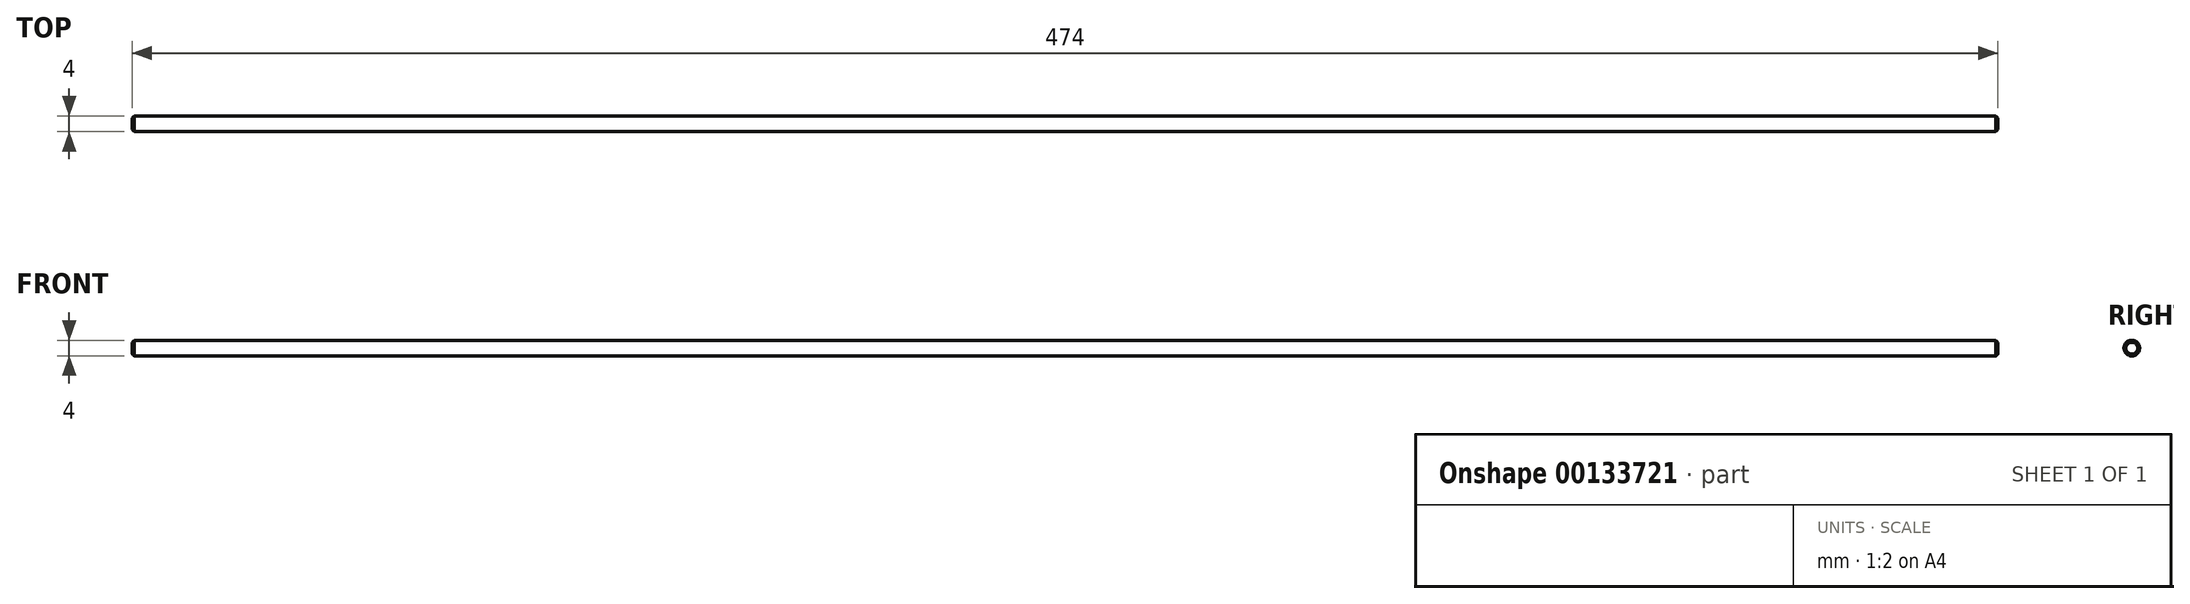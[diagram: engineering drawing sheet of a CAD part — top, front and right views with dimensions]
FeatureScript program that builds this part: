
annotation { "Feature Type Name" : "Feature", "Feature Type Description" : "" }
export const myFeature = defineFeature(function(context is Context, id is Id, definition is map)
    precondition{}
    {
        {
            var Q0;
            Q0=qCreatedBy(makeId("Right.planeOp"),FACE);
            var sketch = newSketch(context, id + "F0", { "sketchPlane" : qUnion([Q0])});
            skCircle(sketch, "E0", {"center": v(0, 0) * mm, "radius": 2 * mm});
            skSolve(sketch);
        }
        {
            var Q0;
            Q0=makeQuery(id+"F0.imprint","IMPRINT",FACE,{"disambiguationData":[TD([[makeQuery(id+"F0.imprint","IMPRINT",EDGE,{"derivedFrom":sQuery(id+"F0.wireOp",EDGE,"E0")}),1.0]])]});
            extrude(context, id + "F1", {"entities" : qUnion([Q0]), "depth" : 474 * mm, "offsetDistance" : 25 * mm, "symmetric" : true});
        }
        {
            var Q0;
            Q0=makeQuery(id+"F1.opExtrude","CAP_EDGE",EDGE,{"disambiguationData":[OSD([sQuery(id+"F0.wireOp",EDGE,"E0")])],"isStart":false});
            var Q1;
            Q1=makeQuery(id+"F1.opExtrude","CAP_EDGE",EDGE,{"disambiguationData":[OSD([sQuery(id+"F0.wireOp",EDGE,"E0")])],"isStart":true});
            chamfer(context, id + "F2", {"entities" : qUnion([Q0, Q1]), "width" : .5 * mm});
        }
    });
